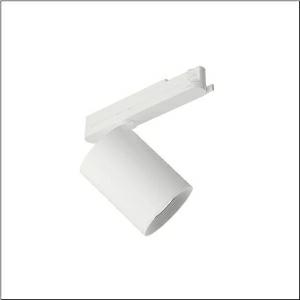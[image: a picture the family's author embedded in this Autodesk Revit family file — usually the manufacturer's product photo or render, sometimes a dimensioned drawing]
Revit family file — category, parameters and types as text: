
# Revit family: spot_21_51se13mbb5b
name_source: partatom
category: Lighting Fixtures
units: mm (PartAtom-declared; Revit-internal decimal feet)

## family parameters
Cut with Voids When Loaded = No
Host = Face
Light Source = No
Part Type = Normal
Room Calculation Point = No
Round Connector Dimension = Use Diameter
Shared = No

## types (1)
- --- (1 x LED, 5350 lm, 41.8 W, 3000K)
    Apparent Load = 42 VA
    CIE Flux Codes = 95 98 99 100 100
    Color Rendering = 90
    Color Temperature = 3000K
    Default Elevation = 1800 mm
    Description = Spot 21, directional spotlight, light control with lens, of PMMA, LED rated luminous flux: 5.140lm, light colour: 930, control gear: ECG Multilumen, with 3-phase adapter, mains connection: 220..240V, AC, 50/60Hz, of aluminium, traffic white (RAL 9016), length: 213mm, diameter: 105mm, protection rating (complete): IP20, insulation class (complete): insulation class I (protective earthing), certification: CE, impact resistance: IK02, permissible ambient temperature for indoor applications: -20..+40°C, packaging unit: 1 piece
    Height = 175 mm
    Lamp = 1 x LED
    Lamp Light Flux = 5350 lm
    Lamp Power = 41.8 W
    Lamp count = 1
    Length = 105 mm
    Luminous efficacy = 128 lm/W
    Manufacturer = Siteco
    ModVariant = No
    Model = 51SE13MBB5B
    Mounting Place = Ceiling
    Mounting Type = Pendant
    Number of Poles = 1
    OnlyDefault = Yes
    Power Factor = 1
    Product Name = Spot 21
    Product group = directional spotlight
    ProductGroupID = 906
    Protection Class = Protection class I
    Protection Degree = IP 20
    RLX_Detail_Level = 1
    RLX_Emergency_Light_Flux = 0 lm
    RLX_Emergency_Type = 0
    RLX_Emergency_Type_DB = No
    RlxData = <blob elided: 17657 chars, md5=574f48e1>
    Socket = socket
    Standby Power = 0 W
    System Light Flux = 5350 lm
    System Power = 42 W
    Type Comments = factory setting: luminous flux: 100 % | (ON | ON | ON | ON) | 1050 mA
    Type Image = l_1003976.jpg
    URL = http://relux.com
    VarID = @adj_144186
    Voltage = 0 V
    Weight = 0.00 kg
    Width = 0 mm  [stored 0 ft]

note: [stored X ft] marks values corroborated as IEEE doubles in the binary element streams (Revit-internal decimal feet)

## geometry (parser evidence)
native form markers: Blend x4, Sweep x9
no freeform markers — native parametric forms only
